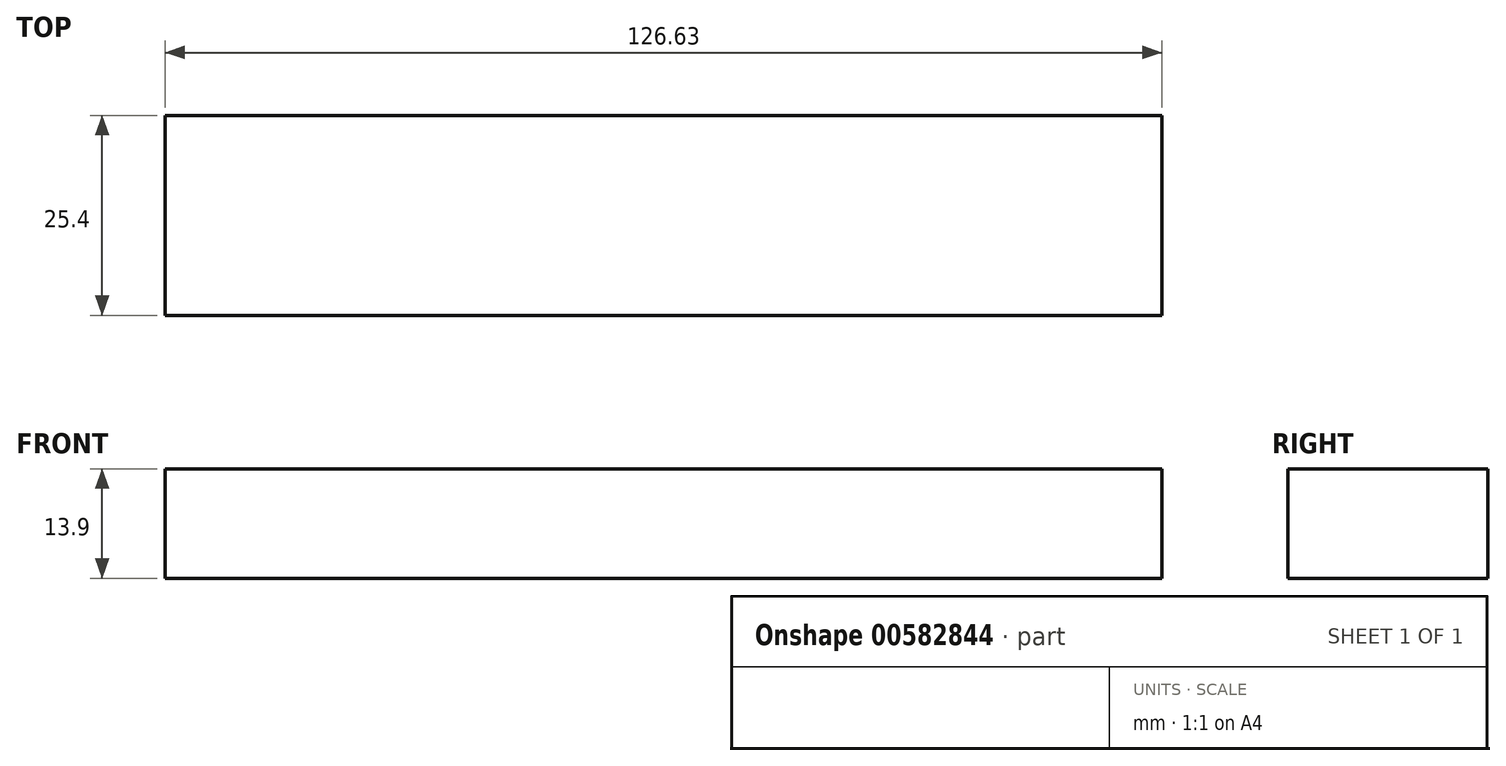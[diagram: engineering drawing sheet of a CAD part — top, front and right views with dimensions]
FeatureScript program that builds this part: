
annotation { "Feature Type Name" : "Feature", "Feature Type Description" : "" }
export const myFeature = defineFeature(function(context is Context, id is Id, definition is map)
    precondition{}
    {
        {
            var Q0;
            Q0=qCreatedBy(makeId("Front.planeOp"),FACE);
            var sketch = newSketch(context, id + "F0", { "sketchPlane" : qUnion([Q0])});
            skLineSegment(sketch, "E0.bottom", {"start": v(-64.47, 56.74) * mm, "end": v(62.16, 56.74) * mm});
            skLineSegment(sketch, "E0.top", {"start": v(-64.47, 42.84) * mm, "end": v(62.16, 42.84) * mm});
            skLineSegment(sketch, "E0.left", {"start": v(-64.47, 56.74) * mm, "end": v(-64.47, 42.84) * mm});
            skLineSegment(sketch, "E0.right", {"start": v(62.16, 56.74) * mm, "end": v(62.16, 42.84) * mm});
            skSolve(sketch);
        }
        {
            var Q0;
            Q0 = qSketchRegion(id + "F0", true);
            extrude(context, id + "F1", {"entities" : qUnion([Q0]), "depth" : 25.4 * mm, "offsetDistance" : 25.4 * mm});
        }
    });
